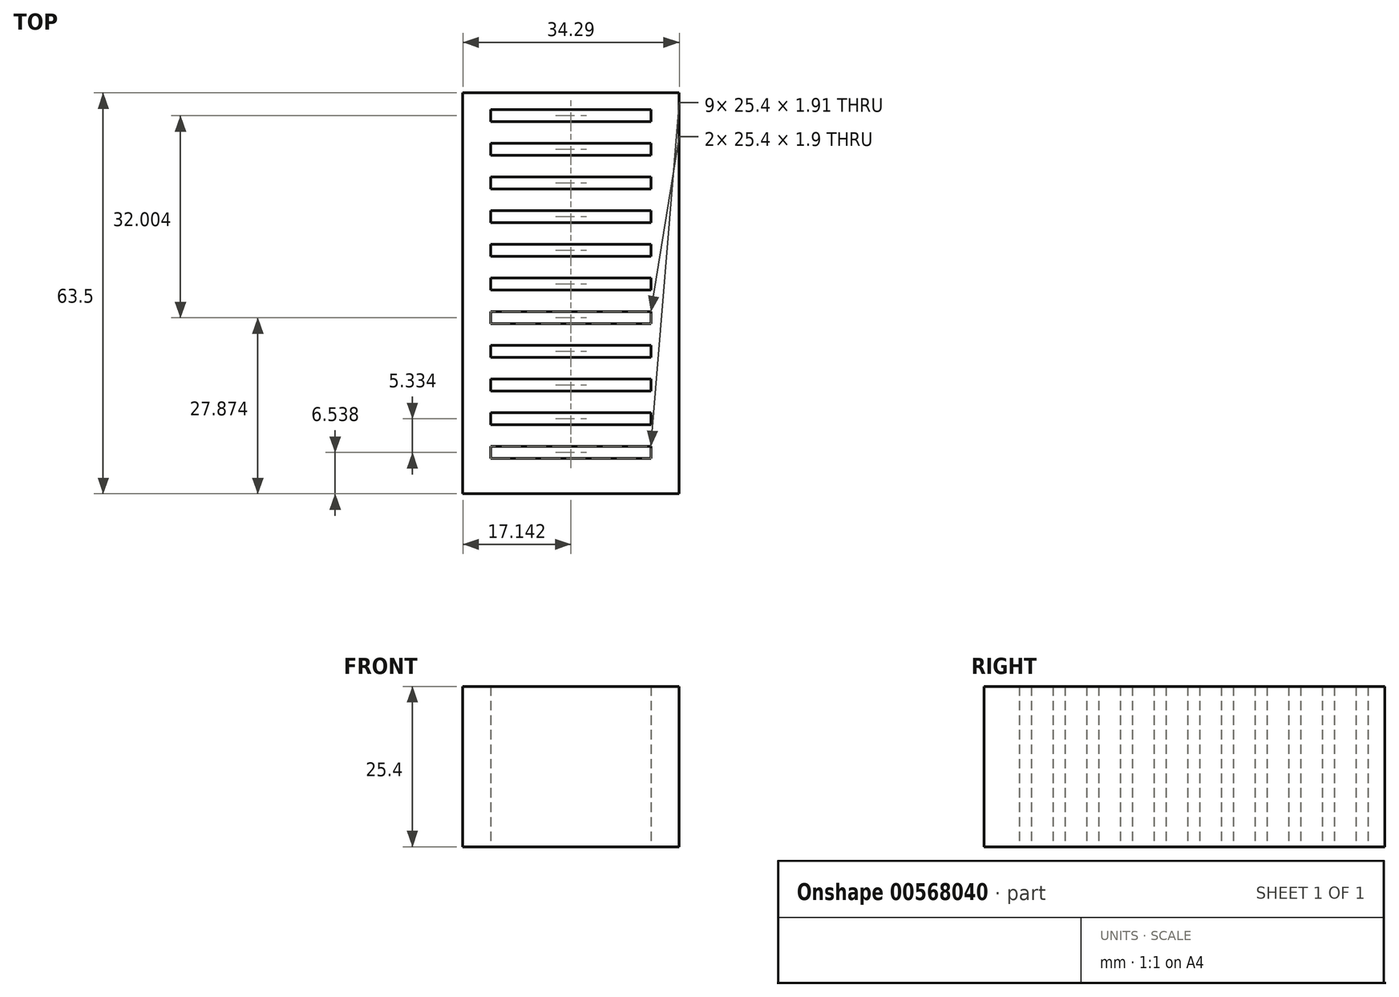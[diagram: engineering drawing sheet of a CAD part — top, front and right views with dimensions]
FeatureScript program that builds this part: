
annotation { "Feature Type Name" : "Feature", "Feature Type Description" : "" }
export const myFeature = defineFeature(function(context is Context, id is Id, definition is map)
    precondition{}
    {
        {
            var Q0;
            Q0=qCreatedBy(makeId("Top.planeOp"),FACE);
            var sketch = newSketch(context, id + "F0", { "sketchPlane" : qUnion([Q0])});
            skLineSegment(sketch, "E0", {"start": v(-10.82, 65.28) * mm, "end": v(23.47, 65.28) * mm});
            skLineSegment(sketch, "E1", {"start": v(23.47, 65.28) * mm, "end": v(23.47, 1.78) * mm});
            skLineSegment(sketch, "E2", {"start": v(23.47, 1.78) * mm, "end": v(-10.82, 1.78) * mm});
            skLineSegment(sketch, "E3", {"start": v(-10.82, 1.78) * mm, "end": v(-10.82, 65.28) * mm});
            skPoint(sketch, "E4.endSnap0", {"position": v(6.32, 1.78) * mm});
            skLineSegment(sketch, "E5", {"start": v(6.32, 7.37) * mm, "end": v(19.02, 7.37) * mm});
            skLineSegment(sketch, "E6", {"start": v(19.02, 7.37) * mm, "end": v(19.02, 9.27) * mm});
            skLineSegment(sketch, "E7", {"start": v(19.02, 9.27) * mm, "end": v(5.65, 9.27) * mm});
            skLineSegment(sketch, "E8", {"start": v(6.32, 7.37) * mm, "end": v(-6.38, 7.37) * mm});
            skLineSegment(sketch, "E9", {"start": v(-6.38, 7.37) * mm, "end": v(-6.38, 9.27) * mm});
            skLineSegment(sketch, "E10", {"start": v(-6.38, 9.27) * mm, "end": v(5.65, 9.27) * mm});
            skPoint(sketch, "E11.start.orphan", {"position": v(6.32, 65.28) * mm});
            skPoint(sketch, "E4.start.orphan", {"position": v(6.32, 1.78) * mm});
            skLineSegment(sketch, "E12", {"start": v(6.32, 12.7) * mm, "end": v(19.02, 12.7) * mm});
            skLineSegment(sketch, "E13", {"start": v(19.02, 12.7) * mm, "end": v(19.02, 14.6) * mm});
            skLineSegment(sketch, "E14", {"start": v(19.02, 14.6) * mm, "end": v(7.88, 14.6) * mm});
            skLineSegment(sketch, "E15", {"start": v(6.32, 12.7) * mm, "end": v(-6.38, 12.7) * mm});
            skLineSegment(sketch, "E16", {"start": v(-6.38, 12.7) * mm, "end": v(-6.38, 14.6) * mm});
            skLineSegment(sketch, "E17", {"start": v(-6.38, 14.6) * mm, "end": v(7.88, 14.6) * mm});
            skLineSegment(sketch, "E18", {"start": v(6.32, 18.03) * mm, "end": v(19.02, 18.03) * mm});
            skLineSegment(sketch, "E19", {"start": v(19.02, 18.03) * mm, "end": v(19.02, 19.94) * mm});
            skLineSegment(sketch, "E20", {"start": v(19.02, 19.94) * mm, "end": v(5.65, 19.94) * mm});
            skLineSegment(sketch, "E21", {"start": v(6.32, 18.03) * mm, "end": v(-6.38, 18.03) * mm});
            skLineSegment(sketch, "E22", {"start": v(-6.38, 18.03) * mm, "end": v(-6.38, 19.94) * mm});
            skLineSegment(sketch, "E23", {"start": v(-6.38, 19.94) * mm, "end": v(5.65, 19.94) * mm});
            skLineSegment(sketch, "E24", {"start": v(6.32, 23.37) * mm, "end": v(19.02, 23.37) * mm});
            skLineSegment(sketch, "E25", {"start": v(19.02, 23.37) * mm, "end": v(19.02, 25.27) * mm});
            skLineSegment(sketch, "E26", {"start": v(19.02, 25.27) * mm, "end": v(5.65, 25.27) * mm});
            skLineSegment(sketch, "E27", {"start": v(6.32, 23.37) * mm, "end": v(-6.38, 23.37) * mm});
            skLineSegment(sketch, "E28", {"start": v(-6.38, 23.37) * mm, "end": v(-6.38, 25.27) * mm});
            skLineSegment(sketch, "E29", {"start": v(-6.38, 25.27) * mm, "end": v(5.65, 25.27) * mm});
            skLineSegment(sketch, "E30", {"start": v(6.32, 28.7) * mm, "end": v(19.02, 28.7) * mm});
            skLineSegment(sketch, "E31", {"start": v(19.02, 28.7) * mm, "end": v(19.02, 30.6) * mm});
            skLineSegment(sketch, "E32", {"start": v(19.02, 30.6) * mm, "end": v(5.65, 30.6) * mm});
            skLineSegment(sketch, "E33", {"start": v(6.32, 28.7) * mm, "end": v(-6.38, 28.7) * mm});
            skLineSegment(sketch, "E34", {"start": v(-6.38, 28.7) * mm, "end": v(-6.38, 30.6) * mm});
            skLineSegment(sketch, "E35", {"start": v(-6.38, 30.6) * mm, "end": v(5.65, 30.6) * mm});
            skLineSegment(sketch, "E36", {"start": v(6.32, 34.04) * mm, "end": v(19.02, 34.04) * mm});
            skLineSegment(sketch, "E37", {"start": v(19.02, 34.04) * mm, "end": v(19.02, 35.94) * mm});
            skLineSegment(sketch, "E38", {"start": v(19.02, 35.94) * mm, "end": v(5.65, 35.94) * mm});
            skLineSegment(sketch, "E39", {"start": v(6.32, 34.04) * mm, "end": v(-6.38, 34.04) * mm});
            skLineSegment(sketch, "E40", {"start": v(-6.38, 34.04) * mm, "end": v(-6.38, 35.94) * mm});
            skLineSegment(sketch, "E41", {"start": v(-6.38, 35.94) * mm, "end": v(5.65, 35.94) * mm});
            skLineSegment(sketch, "E42", {"start": v(6.32, 39.37) * mm, "end": v(19.02, 39.37) * mm});
            skLineSegment(sketch, "E43", {"start": v(19.02, 39.37) * mm, "end": v(19.02, 41.28) * mm});
            skLineSegment(sketch, "E44", {"start": v(19.02, 41.28) * mm, "end": v(5.65, 41.28) * mm});
            skLineSegment(sketch, "E45", {"start": v(6.32, 39.37) * mm, "end": v(-6.38, 39.37) * mm});
            skLineSegment(sketch, "E46", {"start": v(-6.38, 39.37) * mm, "end": v(-6.38, 41.28) * mm});
            skLineSegment(sketch, "E47", {"start": v(-6.38, 41.28) * mm, "end": v(5.65, 41.28) * mm});
            skLineSegment(sketch, "E48", {"start": v(6.32, 44.7) * mm, "end": v(19.02, 44.7) * mm});
            skLineSegment(sketch, "E49", {"start": v(19.02, 44.7) * mm, "end": v(19.02, 46.6) * mm});
            skLineSegment(sketch, "E50", {"start": v(19.02, 46.6) * mm, "end": v(5.65, 46.6) * mm});
            skLineSegment(sketch, "E51", {"start": v(6.32, 44.7) * mm, "end": v(-6.38, 44.7) * mm});
            skLineSegment(sketch, "E52", {"start": v(-6.38, 44.7) * mm, "end": v(-6.38, 46.6) * mm});
            skLineSegment(sketch, "E53", {"start": v(-6.38, 46.6) * mm, "end": v(5.65, 46.6) * mm});
            skLineSegment(sketch, "E54", {"start": v(6.32, 50.04) * mm, "end": v(19.02, 50.04) * mm});
            skLineSegment(sketch, "E55", {"start": v(19.02, 50.04) * mm, "end": v(19.02, 51.94) * mm});
            skLineSegment(sketch, "E56", {"start": v(19.02, 51.94) * mm, "end": v(5.65, 51.94) * mm});
            skLineSegment(sketch, "E57", {"start": v(6.32, 50.04) * mm, "end": v(-6.38, 50.04) * mm});
            skLineSegment(sketch, "E58", {"start": v(-6.38, 50.04) * mm, "end": v(-6.38, 51.94) * mm});
            skLineSegment(sketch, "E59", {"start": v(-6.38, 51.94) * mm, "end": v(5.65, 51.94) * mm});
            skLineSegment(sketch, "E60", {"start": v(6.32, 55.37) * mm, "end": v(19.02, 55.37) * mm});
            skLineSegment(sketch, "E61", {"start": v(19.02, 55.37) * mm, "end": v(19.02, 57.28) * mm});
            skLineSegment(sketch, "E62", {"start": v(19.02, 57.28) * mm, "end": v(5.65, 57.28) * mm});
            skLineSegment(sketch, "E63", {"start": v(6.32, 55.37) * mm, "end": v(-6.38, 55.37) * mm});
            skLineSegment(sketch, "E64", {"start": v(-6.38, 55.37) * mm, "end": v(-6.38, 57.28) * mm});
            skLineSegment(sketch, "E65", {"start": v(-6.38, 57.28) * mm, "end": v(5.65, 57.28) * mm});
            skLineSegment(sketch, "E66", {"start": v(6.32, 60.7) * mm, "end": v(19.02, 60.7) * mm});
            skLineSegment(sketch, "E67", {"start": v(19.02, 60.7) * mm, "end": v(19.02, 62.61) * mm});
            skLineSegment(sketch, "E68", {"start": v(19.02, 62.61) * mm, "end": v(5.65, 62.61) * mm});
            skLineSegment(sketch, "E69", {"start": v(6.32, 60.7) * mm, "end": v(-6.38, 60.7) * mm});
            skLineSegment(sketch, "E70", {"start": v(-6.38, 60.7) * mm, "end": v(-6.38, 62.61) * mm});
            skLineSegment(sketch, "E71", {"start": v(-6.38, 62.61) * mm, "end": v(5.65, 62.61) * mm});
            skSolve(sketch);
        }
        {
            var Q0;
            Q0 = qSketchRegion(id + "F0", true);
            extrude(context, id + "F1", {"entities" : qUnion([Q0]), "depth" : 25.4 * mm, "offsetDistance" : 25.4 * mm});
        }
    });
